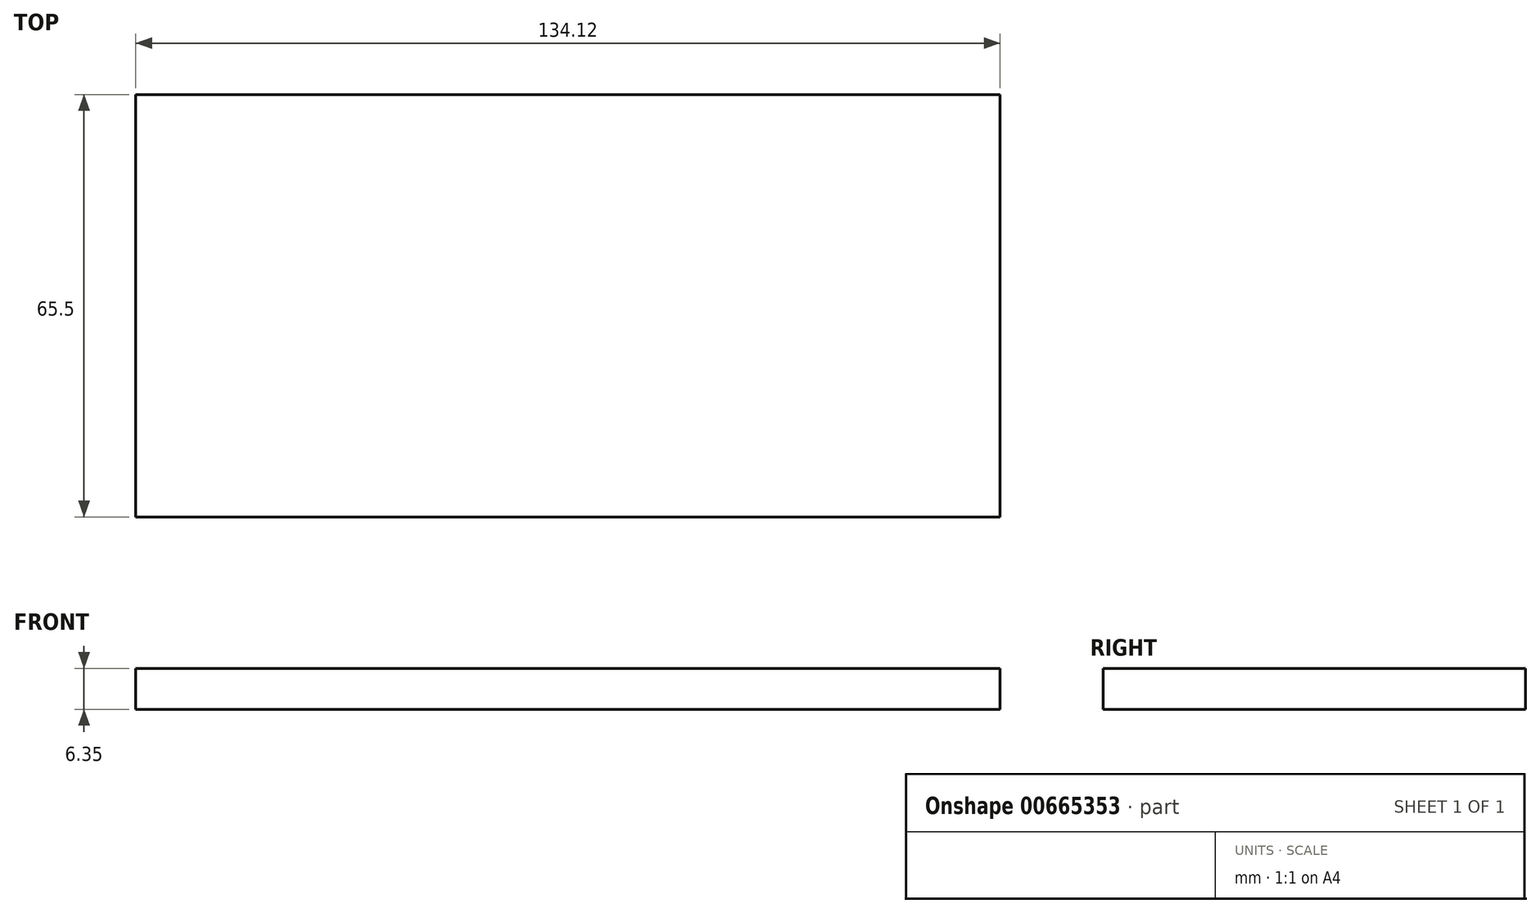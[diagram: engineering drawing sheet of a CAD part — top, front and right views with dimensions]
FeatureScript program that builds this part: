
annotation { "Feature Type Name" : "Feature", "Feature Type Description" : "" }
export const myFeature = defineFeature(function(context is Context, id is Id, definition is map)
    precondition{}
    {
        {
            var Q0;
            Q0=qCreatedBy(makeId("Top.planeOp"),FACE);
            var sketch = newSketch(context, id + "F0", { "sketchPlane" : qUnion([Q0])});
            skLineSegment(sketch, "E0.bottom", {"start": v(67.06, 32.75) * mm, "end": v(-67.06, 32.75) * mm});
            skLineSegment(sketch, "E0.top", {"start": v(67.06, -32.75) * mm, "end": v(-67.06, -32.75) * mm});
            skLineSegment(sketch, "E0.left", {"start": v(67.06, 32.75) * mm, "end": v(67.06, -32.75) * mm});
            skLineSegment(sketch, "E0.right", {"start": v(-67.06, 32.75) * mm, "end": v(-67.06, -32.75) * mm});
            skPoint(sketch, "E0.middle", {"position": v(0, 0) * mm});
            skSolve(sketch);
        }
        {
            var Q0;
            Q0=makeQuery(id+"F0.imprint","IMPRINT",FACE,{"disambiguationData":[TD([[makeQuery(id+"F0.imprint","IMPRINT",EDGE,{"derivedFrom":sQuery(id+"F0.wireOp",EDGE,"E0.bottom")}),1.0]])]});
            extrude(context, id + "F1", {"entities" : qUnion([Q0]), "depth" : 6.35 * mm, "offsetDistance" : 25.4 * mm});
        }
    });
